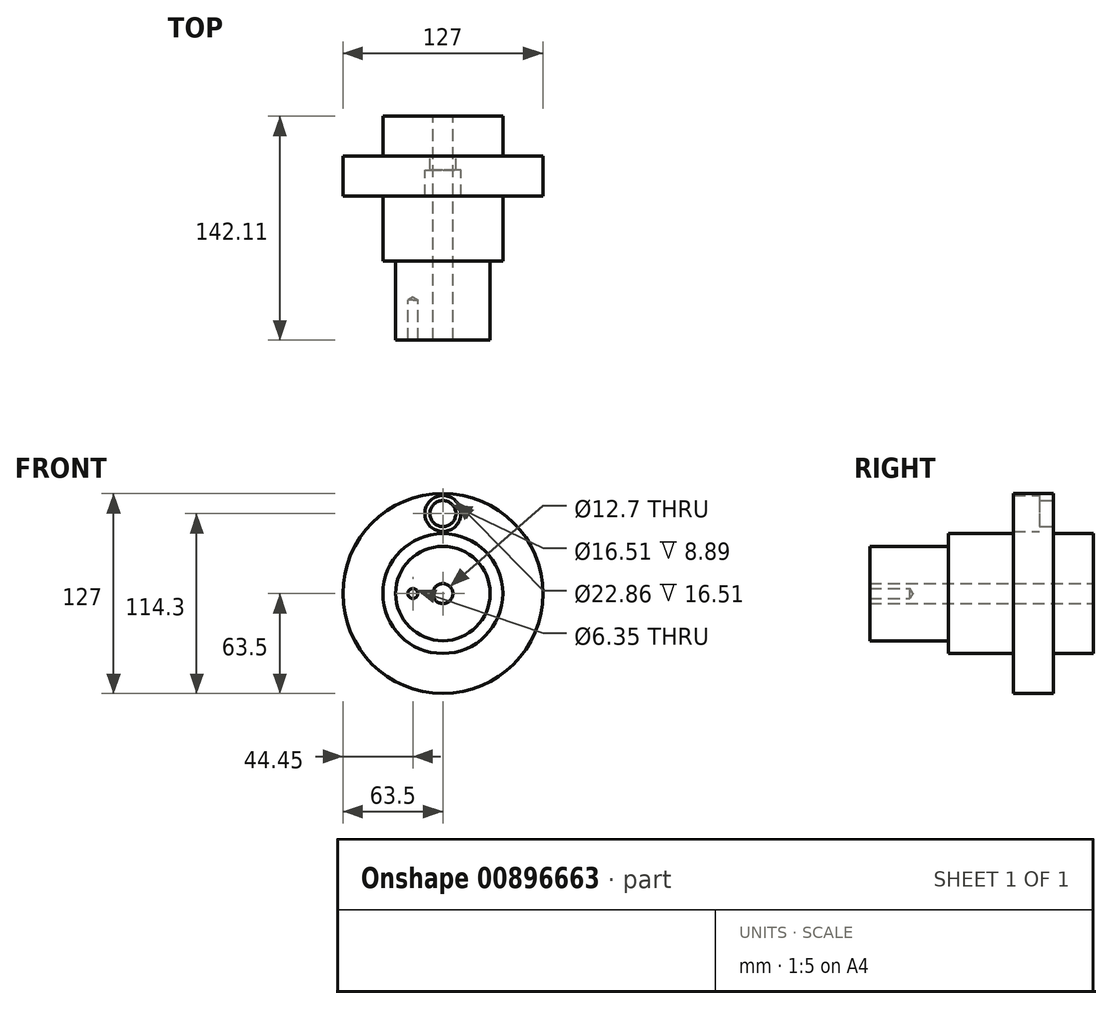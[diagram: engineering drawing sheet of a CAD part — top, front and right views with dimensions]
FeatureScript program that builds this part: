
annotation { "Feature Type Name" : "Feature", "Feature Type Description" : "" }
export const myFeature = defineFeature(function(context is Context, id is Id, definition is map)
    precondition{}
    {
        {
            var Q0;
            Q0=qCreatedBy(makeId("Front.planeOp"),FACE);
            var sketch = newSketch(context, id + "F0", { "sketchPlane" : qUnion([Q0])});
            skCircle(sketch, "E0", {"center": v(0, 0) * mm, "radius": 63.5 * mm});
            skSolve(sketch);
        }
        {
            var Q0;
            Q0=makeQuery(id+"F0.imprint","IMPRINT",FACE,{"disambiguationData":[TD([[makeQuery(id+"F0.imprint","IMPRINT",EDGE,{"derivedFrom":sQuery(id+"F0.wireOp",EDGE,"E0")}),1.0]])]});
            extrude(context, id + "F1", {"entities" : qUnion([Q0]), "depth" : 25.4 * mm, "offsetDistance" : 25.4 * mm});
        }
        {
            var Q0;
            Q0=makeQuery(id+"F1.opExtrude","CAP_FACE",FACE,{"disambiguationData":[OSD([sQuery(id+"F0.wireOp",EDGE,"E0")])],"isStart":false});
            var sketch = newSketch(context, id + "F2", { "sketchPlane" : qUnion([Q0])});
            skCircle(sketch, "E1", {"center": v(0, 0) * mm, "radius": 38.09 * mm});
            skCircle(sketch, "E2", {"center": v(0, 0) * mm, "radius": 50.8 * mm, "construction": true});
            skPoint(sketch, "E3", {"position": v(0, 50.8) * mm});
            skSolve(sketch);
        }
        {
            var Q0;
            Q0=makeQuery(id+"F2.imprint","IMPRINT",FACE,{"disambiguationData":[TD([[makeQuery(id+"F2.imprint","IMPRINT",EDGE,{"derivedFrom":sQuery(id+"F2.wireOp",EDGE,"E1")}),1.0]])]});
            extrude(context, id + "F3", {"entities" : qUnion([Q0]), "operationType" : NewBodyOperationType.ADD, "depth" : 41.27 * mm, "offsetDistance" : 25.4 * mm});
        }
        {
            var Q0;
            Q0=makeQuery(id+"F3.opExtrude","CAP_FACE",FACE,{"disambiguationData":[OSD([sQuery(id+"F2.wireOp",EDGE,"E1")])],"isStart":false});
            var sketch = newSketch(context, id + "F4", { "sketchPlane" : qUnion([Q0])});
            skCircle(sketch, "E4", {"center": v(0, 0) * mm, "radius": 29.98 * mm});
            skSolve(sketch);
        }
        {
            var Q0;
            Q0=makeQuery(id+"F4.imprint","IMPRINT",FACE,{"disambiguationData":[TD([[makeQuery(id+"F4.imprint","IMPRINT",EDGE,{"derivedFrom":sQuery(id+"F4.wireOp",EDGE,"E4")}),1.0]])]});
            extrude(context, id + "F5", {"entities" : qUnion([Q0]), "operationType" : NewBodyOperationType.ADD, "depth" : 50.04 * mm, "offsetDistance" : 25.4 * mm});
        }
        {
            var Q0;
            Q0=makeQuery(id+"F1.opExtrude","CAP_FACE",FACE,{"disambiguationData":[OSD([sQuery(id+"F0.wireOp",EDGE,"E0")])],"isStart":true});
            var sketch = newSketch(context, id + "F6", { "sketchPlane" : qUnion([Q0])});
            skCircle(sketch, "E5", {"center": v(0, 0) * mm, "radius": 38.09 * mm});
            skSolve(sketch);
        }
        {
            var Q0;
            Q0=makeQuery(id+"F6.imprint","IMPRINT",FACE,{"disambiguationData":[TD([[makeQuery(id+"F6.imprint","IMPRINT",EDGE,{"derivedFrom":sQuery(id+"F6.wireOp",EDGE,"E5")}),1.0]])]});
            extrude(context, id + "F7", {"entities" : qUnion([Q0]), "operationType" : NewBodyOperationType.ADD, "depth" : 25.4 * mm, "offsetDistance" : 25.4 * mm});
        }
        {
            var Q0;
            Q0=makeQuery(id+"F7.opExtrude","CAP_FACE",FACE,{"disambiguationData":[OSD([sQuery(id+"F6.wireOp",EDGE,"E5")])],"isStart":false});
            var sketch = newSketch(context, id + "F8", { "sketchPlane" : qUnion([Q0])});
            skCircle(sketch, "E6", {"center": v(0, 0) * mm, "radius": 6.35 * mm});
            skSolve(sketch);
        }
        {
            var Q0;
            Q0=makeQuery(id+"F8.imprint","IMPRINT",FACE,{"disambiguationData":[TD([[makeQuery(id+"F8.imprint","IMPRINT",EDGE,{"derivedFrom":sQuery(id+"F8.wireOp",EDGE,"E6")}),1.0]])]});
            extrude(context, id + "F9", {"entities" : qUnion([Q0]), "operationType" : NewBodyOperationType.REMOVE, "endBound" : BoundingType.THROUGH_ALL, "oppositeDirection" : true, "depth" : 25.4 * mm, "offsetDistance" : 25.4 * mm});
        }
        {
            var Q0;
            Q0=sQuery(id+"F2.wireOp",VERTEX,"E3");
            var Q1;
            Q1=makeQuery(id+"F1.opExtrude","SWEPT_BODY",BODY,{"disambiguationData":[OSD([sQuery(id+"F0.wireOp",EDGE,"E0")])]});
            hole(context, id + "F10", {"style" : HoleStyle.C_BORE, "endStyle" : HoleEndStyle.THROUGH, "holeDiameter" : 16.5 * mm, "cBoreDiameter" : 22.86 * mm, "cBoreDepth" : 16.5 * mm, "majorDiameter" : 6.35 * mm, "isTappedThrough" : true, "tappedDepth" : 12.7 * mm, "tapClearance" : 3, "locations" : qUnion([Q0]), "scope" : qUnion([Q1]), "startStyle" : HoleStartStyle.SKETCH});
        }
        {
            var Q0;
            Q0=makeQuery(id+"F5.opExtrude","CAP_FACE",FACE,{"disambiguationData":[OSD([sQuery(id+"F4.wireOp",EDGE,"E4")])],"isStart":false});
            var sketch = newSketch(context, id + "F11", { "sketchPlane" : qUnion([Q0])});
            skCircle(sketch, "E7", {"center": v(0, 0) * mm, "radius": 19.05 * mm, "construction": true});
            skPoint(sketch, "E8", {"position": v(-19.05, 0) * mm});
            skSolve(sketch);
        }
        {
            var Q0;
            Q0=sQuery(id+"F11.wireOp",VERTEX,"E8");
            var Q1;
            Q1=makeQuery(id+"F1.opExtrude","SWEPT_BODY",BODY,{"disambiguationData":[OSD([sQuery(id+"F0.wireOp",EDGE,"E0")])]});
            hole(context, id + "F12", {"style" : HoleStyle.SIMPLE, "endStyle" : HoleEndStyle.BLIND, "holeDiameter" : 6.35 * mm, "majorDiameter" : 6.35 * mm, "holeDepth" : 25.4 * mm, "isTappedThrough" : true, "tappedDepth" : 12.7 * mm, "tapClearance" : 3, "locations" : qUnion([Q0]), "scope" : qUnion([Q1]), "startStyle" : HoleStartStyle.SKETCH});
        }
    });
